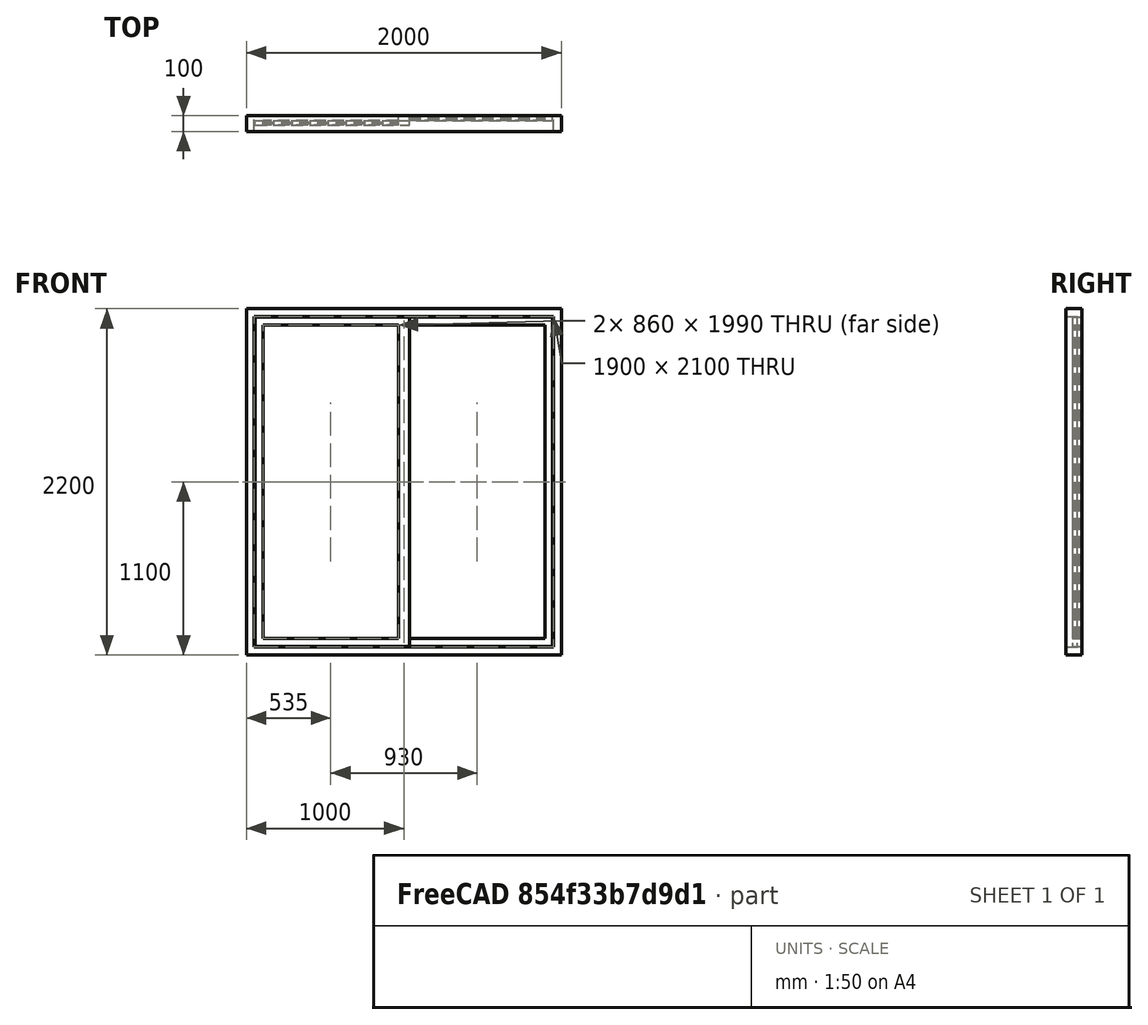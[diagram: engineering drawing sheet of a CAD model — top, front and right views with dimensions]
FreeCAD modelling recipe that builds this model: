
FCSTD DOCUMENT  (FreeCAD 0.16R5636 (Git))
Label: Sliding 2-panes window
License: CC-BY 3.0
LicenseURL: http://creativecommons.org/licenses/by/3.0/
objects: Sketcher::SketchObject×1, Part::FeaturePython×1
note: 2 computed .brp shape members not serialized (recipe doc carries the construction recipe); baked Part::Feature solids carry a one-line shape summary decoded from their .brp

FEATURE [Sketcher::SketchObject] Sketch  label="Sketch2Coulissants"
  Placement = pos=(0,0,0) rot=(1,0,0;1.5708rad)
  sketch-geometry (24):
    g0: LineSegment StartX=0 StartY=0 StartZ=0 EndX=2000 EndY=0 EndZ=0
    g1: LineSegment StartX=2000 StartY=0 StartZ=0 EndX=2000 EndY=2200 EndZ=0
    g2: LineSegment StartX=2000 StartY=2200 StartZ=0 EndX=0 EndY=2200 EndZ=0
    g3: LineSegment StartX=0 StartY=2200 StartZ=0 EndX=0 EndY=0 EndZ=0
    g4: LineSegment StartX=50 StartY=50 StartZ=0 EndX=1950 EndY=50 EndZ=0
    g5: LineSegment StartX=1950 StartY=50 StartZ=0 EndX=1950 EndY=2150 EndZ=0
    g6: LineSegment StartX=1950 StartY=2150 StartZ=0 EndX=50 EndY=2150 EndZ=0
    g7: LineSegment StartX=50 StartY=2150 StartZ=0 EndX=50 EndY=50 EndZ=0
    g8: LineSegment StartX=55 StartY=55 StartZ=0 EndX=1035 EndY=55 EndZ=0
    g9: LineSegment StartX=1035 StartY=55 StartZ=0 EndX=1035 EndY=2145 EndZ=0
    g10: LineSegment StartX=1035 StartY=2145 StartZ=0 EndX=55 EndY=2145 EndZ=0
    g11: LineSegment StartX=55 StartY=2145 StartZ=0 EndX=55 EndY=55 EndZ=0
    g12: LineSegment StartX=105 StartY=105 StartZ=0 EndX=965 EndY=105 EndZ=0
    g13: LineSegment StartX=965 StartY=105 StartZ=0 EndX=965 EndY=2095 EndZ=0
    g14: LineSegment StartX=965 StartY=2095 StartZ=0 EndX=105 EndY=2095 EndZ=0
    g15: LineSegment StartX=105 StartY=2095 StartZ=0 EndX=105 EndY=105 EndZ=0
    g16: LineSegment StartX=965 StartY=55 StartZ=0 EndX=1945 EndY=55 EndZ=0
    g17: LineSegment StartX=1945 StartY=55 StartZ=0 EndX=1945 EndY=2145 EndZ=0
    g18: LineSegment StartX=1945 StartY=2145 StartZ=0 EndX=965 EndY=2145 EndZ=0
    g19: LineSegment StartX=965 StartY=2145 StartZ=0 EndX=965 EndY=55 EndZ=0
    g20: LineSegment StartX=1035 StartY=105 StartZ=0 EndX=1895 EndY=105 EndZ=0
    g21: LineSegment StartX=1895 StartY=105 StartZ=0 EndX=1895 EndY=2095 EndZ=0
    g22: LineSegment StartX=1895 StartY=2095 StartZ=0 EndX=1035 EndY=2095 EndZ=0
    g23: LineSegment StartX=1035 StartY=2095 StartZ=0 EndX=1035 EndY=105 EndZ=0
  constraints (71):
    c: Coincident(g0,g1)
    c: Coincident(g1,g2)
    c: Coincident(g2,g3)
    c: Coincident(g3,g0)
    c: Horizontal(g0)
    c: Horizontal(g2)
    c: Vertical(g1)
    c: Vertical(g3)
    c: Coincident(g4,g5)
    c: Coincident(g5,g6)
    c: Coincident(g6,g7)
    c: Coincident(g7,g4)
    c: Horizontal(g4)
    c: Horizontal(g6)
    c: Vertical(g5)
    c: Vertical(g7)
    c: DistanceY(g1) = 2200
    c: DistanceX(g0) = 2000
    c: DistanceY(g6,g2) = 50
    c: DistanceX(g2,g6) = 50
    c: DistanceX(g4,g0) = 50
    c: DistanceY(g0,g4) = 50
    c: Coincident(g0,g-1)
    c: Coincident(g8,g9)
    c: Coincident(g9,g10)
    c: Coincident(g10,g11)
    c: Coincident(g11,g8)
    c: Horizontal(g8)
    c: Horizontal(g10)
    c: Vertical(g9)
    c: Vertical(g11)
    c: Coincident(g12,g13)
    c: Coincident(g13,g14)
    c: Coincident(g14,g15)
    c: Coincident(g15,g12)
    c: Horizontal(g12)
    c: Horizontal(g14)
    c: Vertical(g13)
    c: Vertical(g15)
    c: Coincident(g16,g17)
    c: Coincident(g17,g18)
    c: Coincident(g18,g19)
    c: Coincident(g19,g16)
    c: Horizontal(g16)
    c: Horizontal(g18)
    c: Vertical(g17)
    c: Vertical(g19)
    c: Coincident(g20,g21)
    c: Coincident(g21,g22)
    c: Coincident(g22,g23)
    c: Coincident(g23,g20)
    c: Horizontal(g20)
    c: Horizontal(g22)
    c: Vertical(g21)
    c: Vertical(g23)
    c: DistanceY(g8,g12) = 50
    c: DistanceX(g8,g12) = 50
    c: DistanceX(g21,g17) = 50
    c: DistanceY(g21,g17) = 50
    c: DistanceX(g14,g10) = 70
    c: DistanceY(g8,g16) = 0
    c: DistanceY(g10,g18) = 0
    c: DistanceX(g4,g8) = 5
    c: DistanceY(g4,g8) = 5
    c: DistanceX(g6,g18) = -5
    c: DistanceY(g6,g18) = -5
    c: PointOnObject(g13,g22)
    c: PointOnObject(g20,g12)
    c: PointOnObject(g13,g19)
    c: PointOnObject(g22,g9)
    c: Equal(g22,g14)
FEATURE [Part::FeaturePython] Fen__tre  label="Fenetre2Coulissants"  # WARN: FeaturePython — macro-defined, semantics opaque (R4)
  Base = -> Sketch
  Height = 2200
  HoleDepth = 0
  Normal = (0,1,0)
  Preset = 5
  Role = 0
  Width = 2000
  WindowParts = OuterFrame | Frame | Wire0,Wire1 | 100.0 | 0.0 | LeftFrame | Frame | Wire2,Wire3 | 30.0 | 40.0 | LeftGlass | Glass panel | Wire3 | 10.0 | 50.0 | RightFrame | Frame | Wire4,Wire5 | 30.0 | 70.0 | RightGlass | Glass panel | Wire5 | 10.0 | 80.0
